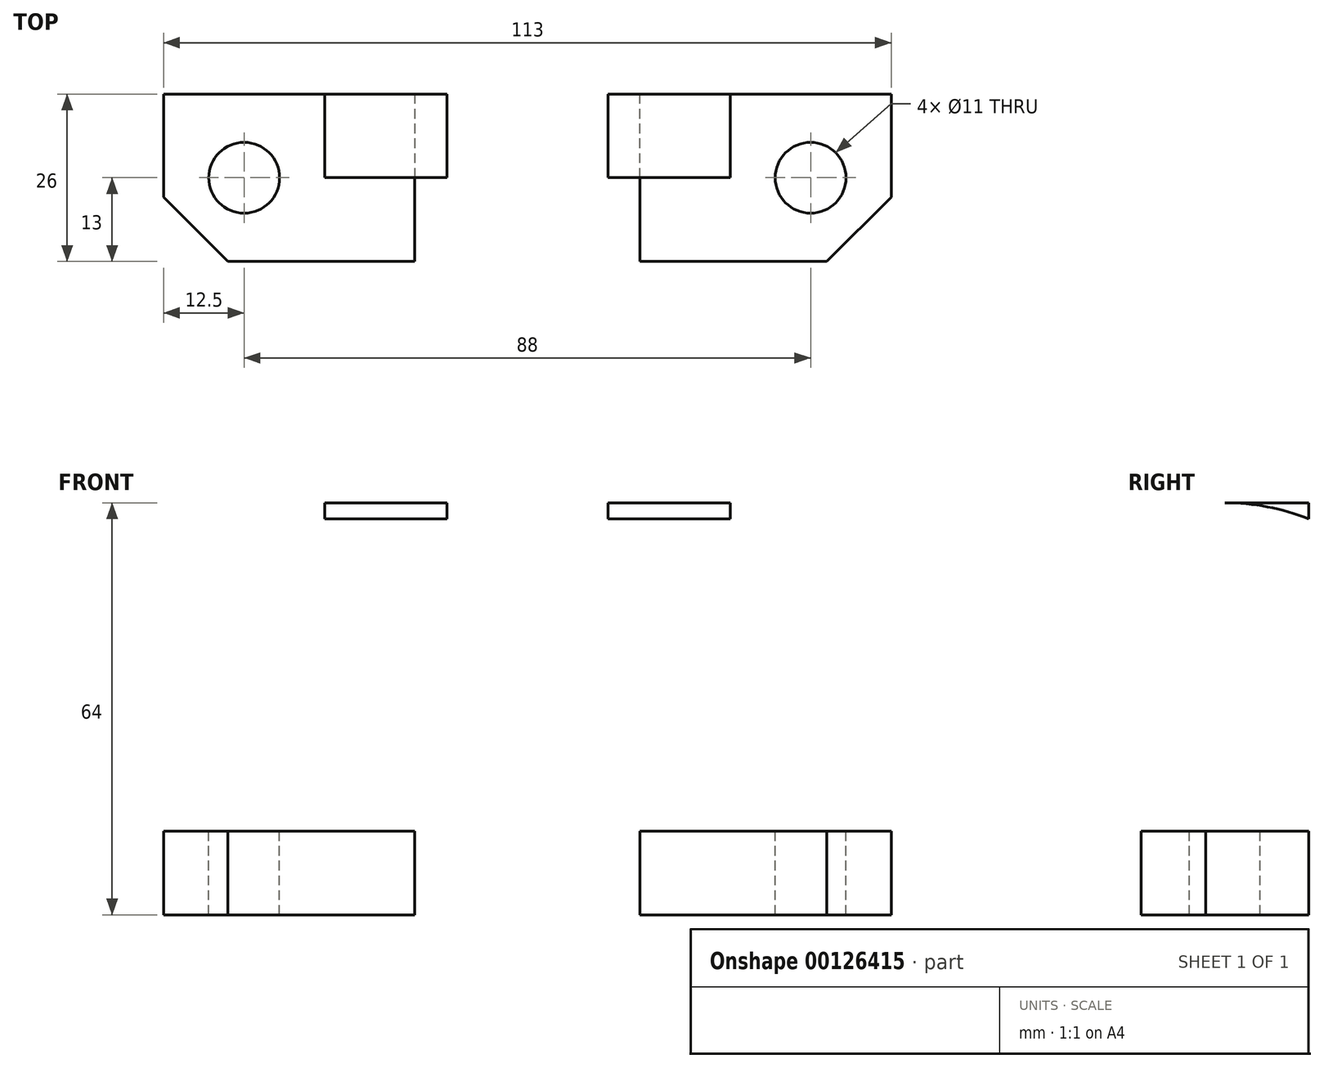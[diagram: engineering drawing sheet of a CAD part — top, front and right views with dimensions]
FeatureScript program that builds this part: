
annotation { "Feature Type Name" : "Feature", "Feature Type Description" : "" }
export const myFeature = defineFeature(function(context is Context, id is Id, definition is map)
    precondition{}
    {
        {
            var Q0;
            Q0=qCreatedBy(makeId("Front.planeOp"),FACE);
            var sketch = newSketch(context, id + "F0", { "sketchPlane" : qUnion([Q0])});
            skLineSegment(sketch, "E0", {"start": v(0, 0) * mm, "end": v(10, 0) * mm});
            skLineSegment(sketch, "E1", {"start": v(10, 0) * mm, "end": v(39, 0) * mm});
            skLineSegment(sketch, "E2", {"start": v(39, 0) * mm, "end": v(39, 17) * mm});
            skLineSegment(sketch, "E3", {"start": v(39, 17) * mm, "end": v(74, 17) * mm});
            skLineSegment(sketch, "E4", {"start": v(74, 17) * mm, "end": v(74, 0) * mm});
            skLineSegment(sketch, "E5", {"start": v(74, 0) * mm, "end": v(103, 0) * mm});
            skLineSegment(sketch, "E6", {"start": v(103, 0) * mm, "end": v(113, 0) * mm});
            skLineSegment(sketch, "E7", {"start": v(113, 0) * mm, "end": v(113, 13) * mm});
            skLineSegment(sketch, "E8", {"start": v(113, 13) * mm, "end": v(88, 13) * mm});
            skLineSegment(sketch, "E9", {"start": v(88, 13) * mm, "end": v(88, 64) * mm});
            skLineSegment(sketch, "E10", {"start": v(88, 64) * mm, "end": v(69, 64) * mm});
            skLineSegment(sketch, "E11", {"start": v(69, 64) * mm, "end": v(69, 30) * mm});
            skLineSegment(sketch, "E12", {"start": v(69, 30) * mm, "end": v(44, 30) * mm});
            skLineSegment(sketch, "E13", {"start": v(44, 30) * mm, "end": v(44, 64) * mm});
            skLineSegment(sketch, "E14", {"start": v(44, 64) * mm, "end": v(25, 64) * mm});
            skLineSegment(sketch, "E15", {"start": v(25, 64) * mm, "end": v(25, 13) * mm});
            skLineSegment(sketch, "E16", {"start": v(25, 13) * mm, "end": v(0, 13) * mm});
            skLineSegment(sketch, "E17", {"start": v(0, 13) * mm, "end": v(0, 0) * mm});
            skLineSegment(sketch, "E18", {"start": v(10, 0) * mm, "end": v(10, 13) * mm});
            skLineSegment(sketch, "E19", {"start": v(103, 0) * mm, "end": v(103, 13) * mm});
            skSolve(sketch);
        }
        {
            var Q0;
            Q0 = qSketchRegion(id + "F0", true);
            var Q1;
            Q1=makeQuery(id+"F0.imprint","IMPRINT",FACE,{"disambiguationData":[TD([[makeQuery(id+"F0.imprint","IMPRINT",EDGE,{"derivedFrom":sQuery(id+"F0.wireOp",EDGE,"E1")}),1.0]])]});
            extrude(context, id + "F1", {"entities" : qUnion([Q0, Q1]), "endBound" : BoundingType.SYMMETRIC, "depth" : 26 * mm});
        }
        {
            var Q0;
            Q0=makeQuery(id+"F1.opExtrude","SWEPT_FACE",FACE,{"disambiguationData":[OSD([sQuery(id+"F0.wireOp",EDGE,"E16")])]});
            var sketch = newSketch(context, id + "F2", { "sketchPlane" : qUnion([Q0])});
            skLineSegment(sketch, "E20", {"start": v(10, -13) * mm, "end": v(0, -3) * mm});
            skLineSegment(sketch, "E21", {"start": v(0, 0) * mm, "end": v(25, 0) * mm, "construction": true});
            skLineSegment(sketch, "E22", {"start": v(12.5, 13) * mm, "end": v(12.5, -13) * mm, "construction": true});
            skCircle(sketch, "E23", {"center": v(12.5, 0) * mm, "radius": 5.5 * mm});
            skSolve(sketch);
        }
        {
            var Q0;
            {var subQ0=sQuery(id+"F2.wireOp",EDGE,"E20");Q0=makeQuery(id+"F2.imprint","IMPRINT",FACE,{"disambiguationData":[TD([[makeQuery(id+"F2.imprint","IMPRINT",EDGE,{"derivedFrom":subQ0}),1.0]])]});}
            var Q1;
            Q1=makeQuery(id+"F2.imprint","IMPRINT",FACE,{"disambiguationData":[TD([[makeQuery(id+"F2.imprint","IMPRINT",EDGE,{"derivedFrom":sQuery(id+"F2.wireOp",EDGE,"E23")}),1.0]])]});
            extrude(context, id + "F3", {"entities" : qUnion([Q0, Q1]), "operationType" : NewBodyOperationType.REMOVE, "endBound" : BoundingType.THROUGH_ALL, "oppositeDirection" : true, "depth" : 25 * mm});
        }
        {
            var Q0;
            Q0=makeQuery(id+"F1.opExtrude","SWEPT_FACE",FACE,{"disambiguationData":[OSD([sQuery(id+"F0.wireOp",EDGE,"E8")])]});
            var sketch = newSketch(context, id + "F4", { "sketchPlane" : qUnion([Q0])});
            skLineSegment(sketch, "E24", {"start": v(103, -13) * mm, "end": v(113, -3) * mm});
            skLineSegment(sketch, "E25", {"start": v(88, 0) * mm, "end": v(113, 0) * mm, "construction": true});
            skLineSegment(sketch, "E26", {"start": v(100.5, -13) * mm, "end": v(100.5, 13) * mm, "construction": true});
            skCircle(sketch, "E27", {"center": v(100.5, 0) * mm, "radius": 5.5 * mm});
            skSolve(sketch);
        }
        {
            var Q0;
            Q0 = qSketchRegion(id + "F4", true);
            var Q1;
            {var subQ0=sQuery(id+"F4.wireOp",EDGE,"E24");Q1=makeQuery(id+"F4.imprint","IMPRINT",FACE,{"disambiguationData":[TD([[makeQuery(id+"F4.imprint","IMPRINT",EDGE,{"derivedFrom":subQ0}),-1.0]])]});}
            extrude(context, id + "F5", {"entities" : qUnion([Q0, Q1]), "operationType" : NewBodyOperationType.REMOVE, "endBound" : BoundingType.THROUGH_ALL, "oppositeDirection" : true, "depth" : 25 * mm});
        }
        {
            var Q0;
            Q0=makeQuery(id+"F1.opExtrude","SWEPT_FACE",FACE,{"disambiguationData":[OSD([sQuery(id+"F0.wireOp",EDGE,"E9")])]});
            var sketch = newSketch(context, id + "F6", { "sketchPlane" : qUnion([Q0])});
            skLineSegment(sketch, "E28.0", {"start": v(-3, 0) * mm, "end": v(13, 0) * mm});
            skLineSegment(sketch, "E29.0", {"start": v(-13, 0) * mm, "end": v(-3, 0) * mm});
            skCircle(sketch, "E30", {"center": v(0, 46) * mm, "radius": 6.5 * mm});
            skPoint(sketch, "E30.centerSnap0", {"position": v(0, 64) * mm});
            skArc(sketch, "E31", {"start": v(0, 64) * mm, "mid": v(6.62, 63.37) * mm, "end": v(13, 61.5) * mm});
            skArc(sketch, "E32", {"start": v(0, 64) * mm, "mid": v(-6.62, 63.37) * mm, "end": v(-13, 61.5) * mm});
            skSolve(sketch);
        }
        {
            var Q0;
            Q0 = qSketchRegion(id + "F6", true);
            var Q1;
            Q1=makeQuery(id+"F6.imprint","IMPRINT",FACE,{"disambiguationData":[TD([[makeQuery(id+"F6.imprint","IMPRINT",EDGE,{"derivedFrom":sQuery(id+"F6.wireOp",EDGE,"E30")}),1.0]])]});
            extrude(context, id + "F7", {"entities" : qUnion([Q0, Q1]), "operationType" : NewBodyOperationType.REMOVE, "endBound" : BoundingType.THROUGH_ALL, "oppositeDirection" : true, "depth" : 25 * mm});
        }
        {
            var Q0;
            {var subQ0=sQuery(id+"F6.wireOp",EDGE,"E31");Q0=makeQuery(id+"F6.imprint","IMPRINT",FACE,{"disambiguationData":[TD([[makeQuery(id+"F6.imprint","IMPRINT",EDGE,{"derivedFrom":subQ0}),1.0]])]});}
            var Q1;
            {var subQ0=sQuery(id+"F6.wireOp",EDGE,"E32");Q1=makeQuery(id+"F6.imprint","IMPRINT",FACE,{"disambiguationData":[TD([[makeQuery(id+"F6.imprint","IMPRINT",EDGE,{"derivedFrom":subQ0}),-1.0]])]});}
            extrude(context, id + "F8", {"entities" : qUnion([Q0, Q1]), "operationType" : NewBodyOperationType.REMOVE, "endBound" : BoundingType.THROUGH_ALL, "oppositeDirection" : true, "depth" : 25 * mm});
        }
    });
